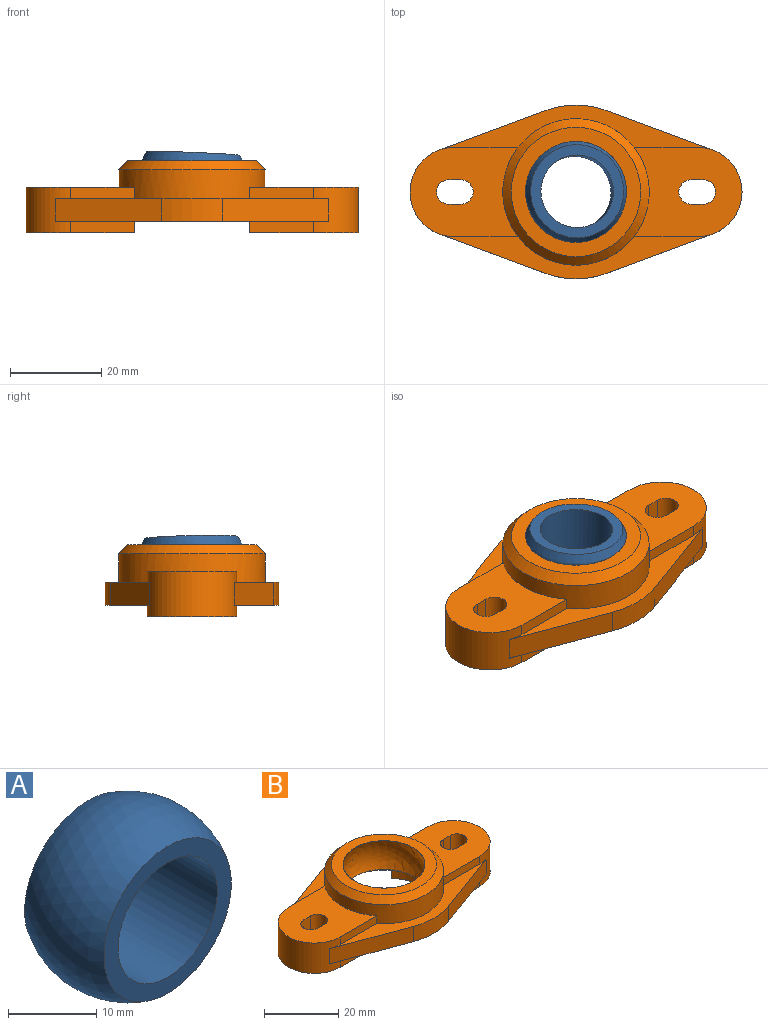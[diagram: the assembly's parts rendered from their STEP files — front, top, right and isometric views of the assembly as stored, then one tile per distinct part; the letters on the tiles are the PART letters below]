
ASSEMBLY  parts=2 mates=1
PART A: 4 faces, bbox 24x12.7x24 mm
  f0: sphere r=12mm, area 957.6mm2, adj f1,f2
  f1: plane 20.37x20.37mm, normal (0,-1,0), area 127.8mm2, adj f0,f3
  f2: plane 20.37x20.37mm, normal (0,1,0), area 127.8mm2, adj f0,f3
  f3: cylinder r=7.94mm len=15.88mm, axis (0,-1,0), area 633.4mm2, adj f1,f2
PART B: 43 faces, bbox 72.6x38x24 mm
  f0: cylinder r=11.03mm len=22.06mm, axis (0,0,1), area 1.7mm2, adj f35,f42
  f1: cylinder r=11.03mm len=22.06mm, axis (0,0,1), area 1.7mm2, adj f39,f42
  f2: plane 59.81x9.81mm, normal (0,0,-1), area 180.9mm2, adj f5,f16,f18,f19,f28,f29,f30,f38
  f3: plane 59.81x9.81mm, normal (0,0,-1), area 180.9mm2, adj f4,f15,f18,f19,f31,f32,f33,f38
  f4: plane 13.86x2.5mm, normal (0,-1,0), area 34.6mm2, adj f3,f17,f18,f37
  f5: plane 13.86x2.5mm, normal (0,1,0), area 34.6mm2, adj f2,f6,f19,f36
  f6: plane 23.66x19.6mm, normal (0,0,-1), area 340.8mm2, adj f5,f15,f19,f20,f21,f22,f23,f36
  f7: plane 23.65x19.6mm, normal (0,0,1), area 340.7mm2, adj f10,f11,f18,f24,f25,f26,f27,f34
  f8: plane 23.65x19.6mm, normal (0,0,1), area 340.7mm2, adj f9,f12,f19,f20,f21,f22,f23,f34
  f9: plane 13.85x2.5mm, normal (0,-1,0), area 34.6mm2, adj f8,f14,f19,f34
  f10: plane 13.85x2.5mm, normal (0,-1,0), area 34.6mm2, adj f7,f14,f18,f34
  f11: plane 13.85x2.5mm, normal (0,1,0), area 34.6mm2, adj f7,f13,f18,f34
  f12: plane 13.85x2.5mm, normal (0,1,0), area 34.6mm2, adj f8,f13,f19,f34
  f13: plane 59.81x9.81mm, normal (0,0,1), area 180.8mm2, adj f11,f12,f18,f19,f28,f29,f30,f34
  f14: plane 59.81x9.81mm, normal (0,0,1), area 180.8mm2, adj f9,f10,f18,f19,f31,f32,f33,f34
  f15: plane 13.86x2.5mm, normal (0,-1,0), area 34.6mm2, adj f3,f6,f19,f36
  f16: plane 13.86x2.5mm, normal (0,1,0), area 34.6mm2, adj f2,f17,f18,f37
  f17: plane 23.66x19.6mm, normal (0,0,-1), area 340.8mm2, adj f4,f16,f18,f24,f25,f26,f27,f37
  f18: cylinder r=9.8mm len=19.6mm, axis (0,0,-1), area 273.1mm2, adj f2,f3,f4,f7,f10,f11,f13,f14
  f19: cylinder r=9.8mm len=19.6mm, axis (0,0,-1), area 273.1mm2, adj f2,f3,f5,f6,f8,f9,f12,f13
  f20: cylinder r=2.69mm len=10mm, axis (0,0,-1), area 84.6mm2, adj f6,f8,f21,f23
  f21: plane 10x2.62mm, normal (0,1,0), area 26.2mm2, adj f6,f8,f20,f22
  f22: cylinder r=2.69mm len=10mm, axis (0,0,-1), area 84.6mm2, adj f6,f8,f21,f23
  f23: plane 10x2.62mm, normal (0,-1,0), area 26.2mm2, adj f6,f8,f20,f22
  f24: cylinder r=2.69mm len=10mm, axis (0,0,-1), area 84.6mm2, adj f7,f17,f25,f27
  f25: plane 10x2.62mm, normal (0,1,0), area 26.2mm2, adj f7,f17,f24,f26
  f26: cylinder r=2.69mm len=10mm, axis (0,0,-1), area 84.6mm2, adj f7,f17,f25,f27
  f27: plane 10x2.62mm, normal (0,-1,0), area 26.2mm2, adj f7,f17,f24,f26
  f28: cylinder r=19mm len=13.19mm, axis (0,0,-1), area 67.4mm2, adj f2,f13,f29,f30
  f29: plane 23.31x8.63mm, normal (0.35,0.94,0), area 124.3mm2, adj f2,f13,f19,f28
  f30: plane 23.31x8.63mm, normal (-0.35,0.94,0), area 124.3mm2, adj f2,f13,f18,f28
  f31: plane 23.31x8.63mm, normal (-0.35,-0.94,0), area 124.3mm2, adj f3,f14,f18,f32
  f32: cylinder r=19mm len=13.19mm, axis (0,0,-1), area 67.4mm2, adj f3,f14,f31,f33
  f33: plane 23.31x8.63mm, normal (0.35,-0.94,0), area 124.3mm2, adj f3,f14,f19,f32
  f34: cylinder r=16mm len=32mm, axis (0,0,-1), area 523.1mm2, adj f7,f8,f9,f10,f11,f12,f13,f14
  f35: plane 28.29x28.29mm, normal (0,0,1), area 246.4mm2, adj f0,f41
  f36: cylinder r=16mm len=19.6mm, axis (0,0,-1), area 52.7mm2, adj f5,f6,f15,f38
  f37: cylinder r=16mm len=19.6mm, axis (0,0,-1), area 52.7mm2, adj f4,f16,f17,f38
  f38: cone r=16mm half-angle=42.7deg, axis (0,0,-1), area 457.5mm2, adj f2,f3,f36,f37,f40
  f39: plane 25.08x25.08mm, normal (0,0,-1), area 111.6mm2, adj f1,f40
  f40: cylinder r=12.54mm len=25.08mm, axis (0,0,-1), area 0.2mm2, adj f38,f39
  f41: cone r=14.15mm half-angle=42.9deg, axis (0,0,-1), area 258.4mm2, adj f34,f35
  f42: sphere r=12mm, area 712.7mm2, adj f0,f1
PLACE A rot(axis=(-1,0.03,0.01),91.4deg) t=(0,0,6)mm
PLACE B at identity fixed
MATE ball A.f3 <-> B.f0  axis (0.04,0.02,1) through (0,0,6)mm
